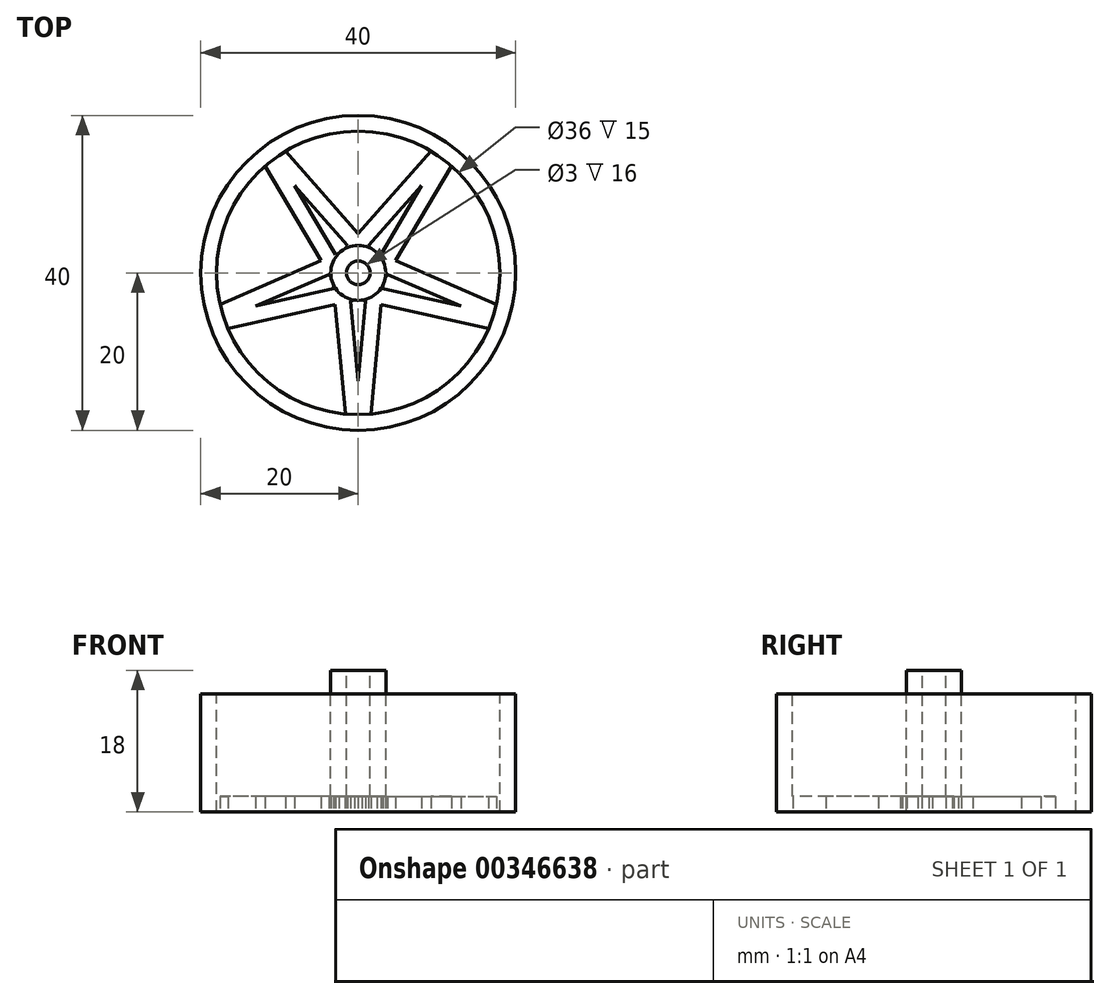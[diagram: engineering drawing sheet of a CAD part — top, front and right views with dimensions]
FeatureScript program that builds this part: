
annotation { "Feature Type Name" : "Feature", "Feature Type Description" : "" }
export const myFeature = defineFeature(function(context is Context, id is Id, definition is map)
    precondition{}
    {
        {
            var Q0;
            Q0=qCreatedBy(makeId("Top.planeOp"),FACE);
            var sketch = newSketch(context, id + "F0", { "sketchPlane" : qUnion([Q0])});
            skCircle(sketch, "E0", {"center": v(0, 0) * mm, "radius": 20 * mm});
            skSolve(sketch);
        }
        {
            var Q0;
            Q0=makeQuery(id+"F0.imprint","IMPRINT",FACE,{"disambiguationData":[TD([[makeQuery(id+"F0.imprint","IMPRINT",EDGE,{"derivedFrom":sQuery(id+"F0.wireOp",EDGE,"E0")}),1.0]])]});
            extrude(context, id + "F1", {"entities" : qUnion([Q0]), "depth" : 15 * mm});
        }
        {
            var Q0;
            Q0=makeQuery(id+"F1.opExtrude","CAP_FACE",FACE,{"disambiguationData":[OSD([sQuery(id+"F0.wireOp",EDGE,"E0")])],"isStart":false});
            var sketch = newSketch(context, id + "F2", { "sketchPlane" : qUnion([Q0])});
            skCircle(sketch, "E1", {"center": v(0, 0) * mm, "radius": 18 * mm});
            skSolve(sketch);
        }
        {
            var Q0;
            Q0=makeQuery(id+"F2.imprint","IMPRINT",FACE,{"disambiguationData":[TD([[makeQuery(id+"F2.imprint","IMPRINT",EDGE,{"derivedFrom":sQuery(id+"F2.wireOp",EDGE,"E1")}),1.0]])]});
            extrude(context, id + "F3", {"entities" : qUnion([Q0]), "operationType" : NewBodyOperationType.REMOVE, "oppositeDirection" : true, "depth" : 13 * mm});
        }
        {
            var Q0;
            Q0=makeQuery(id+"F2.imprint","IMPRINT",FACE,{"disambiguationData":[TD([[makeQuery(id+"F2.imprint","IMPRINT",EDGE,{"derivedFrom":sQuery(id+"F2.wireOp",EDGE,"E1")}),1.0]])]});
            var sketch = newSketch(context, id + "F4", { "sketchPlane" : qUnion([Q0])});
            skCircle(sketch, "E2", {"center": v(0, 0) * mm, "radius": 3.5 * mm});
            skCircle(sketch, "E3", {"center": v(0, 0) * mm, "radius": 1.5 * mm});
            skSolve(sketch);
        }
        {
            var Q0;
            Q0=makeQuery(id+"F4.imprint","IMPRINT",FACE,{"disambiguationData":[TD([[makeQuery(id+"F4.imprint","IMPRINT",EDGE,{"derivedFrom":sQuery(id+"F4.wireOp",EDGE,"E2")}),1.0]])]});
            extrude(context, id + "F5", {"entities" : qUnion([Q0]), "operationType" : NewBodyOperationType.ADD, "oppositeDirection" : true, "depth" : 13 * mm});
        }
        {
            var Q0;
            Q0=makeQuery(id+"F2.imprint","IMPRINT",FACE,{"disambiguationData":[TD([[makeQuery(id+"F2.imprint","IMPRINT",EDGE,{"derivedFrom":sQuery(id+"F2.wireOp",EDGE,"E1")}),1.0]])]});
            var sketch = newSketch(context, id + "F6", { "sketchPlane" : qUnion([Q0])});
            skCircle(sketch, "E4", {"center": v(0, 0) * mm, "radius": 1.5 * mm});
            skCircle(sketch, "E5", {"center": v(0, 0) * mm, "radius": 3.5 * mm});
            skSolve(sketch);
        }
        {
            var Q0;
            Q0=makeQuery(id+"F6.imprint","IMPRINT",FACE,{"disambiguationData":[TD([[makeQuery(id+"F6.imprint","IMPRINT",EDGE,{"derivedFrom":sQuery(id+"F6.wireOp",EDGE,"E4")}),-1.0]])]});
            extrude(context, id + "F7", {"entities" : qUnion([Q0]), "operationType" : NewBodyOperationType.ADD, "depth" : 3 * mm});
        }
        {
            var Q0;
            Q0=makeQuery(id+"F1.opExtrude","CAP_FACE",FACE,{"disambiguationData":[OSD([sQuery(id+"F0.wireOp",EDGE,"E0")])],"isStart":true});
            var sketch = newSketch(context, id + "F8", { "sketchPlane" : qUnion([Q0])});
            skSolve(sketch);
        }
        {
            var Q0;
            Q0=makeQuery(id+"F8.imprint","IMPRINT",FACE,{"disambiguationData":[TD([[makeQuery(id+"F8.imprint","IMPRINT",EDGE,{"derivedFrom":makeQuery(id+"F1.opExtrude","CAP_EDGE",EDGE,{"disambiguationData":[OSD([sQuery(id+"F0.wireOp",EDGE,"E0")])],"isStart":true})}),-1.0]])]});
            var sketch = newSketch(context, id + "F9", { "sketchPlane" : qUnion([Q0])});
            skCircle(sketch, "E6", {"center": v(0, 0) * mm, "radius": 3.5 * mm});
            skCircle(sketch, "E7", {"center": v(0, 0) * mm, "radius": 18 * mm});
            skLineSegment(sketch, "E8", {"start": v(-3.15, 1.52) * mm, "end": v(-3.1, 2.01) * mm});
            skLineSegment(sketch, "E9.MirrorCS", {"start": v(3.15, 1.52) * mm, "end": v(3.1, 2.01) * mm});
            skLineSegment(sketch, "E10.0", {"start": v(-0.97, 3.36) * mm, "end": v(0, 13.72) * mm});
            skLineSegment(sketch, "E11.0", {"start": v(0.97, 3.36) * mm, "end": v(0, 13.72) * mm});
            skLineSegment(sketch, "E12.1.0", {"start": v(-0.47, 3.47) * mm, "end": v(-0.95, 3.58) * mm});
            skLineSegment(sketch, "E12.1.1", {"start": v(-2.9, 1.96) * mm, "end": v(-13.05, 4.24) * mm});
            skLineSegment(sketch, "E12.1.2", {"start": v(-3.5, 0.11) * mm, "end": v(-13.05, 4.24) * mm});
            skLineSegment(sketch, "E12.1.3", {"start": v(-2.42, -2.53) * mm, "end": v(-2.87, -2.33) * mm});
            skLineSegment(sketch, "E12.2.0", {"start": v(-3.44, 0.63) * mm, "end": v(-3.7, 0.2) * mm});
            skLineSegment(sketch, "E12.2.1", {"start": v(-2.76, -2.15) * mm, "end": v(-8.07, -11.1) * mm});
            skLineSegment(sketch, "E12.2.2", {"start": v(-1.2, -3.3) * mm, "end": v(-8.07, -11.1) * mm});
            skLineSegment(sketch, "E12.2.3", {"start": v(1.66, -3.08) * mm, "end": v(1.33, -3.45) * mm});
            skLineSegment(sketch, "E12.3.0", {"start": v(-1.66, -3.08) * mm, "end": v(-1.33, -3.45) * mm});
            skLineSegment(sketch, "E12.3.1", {"start": v(1.2, -3.3) * mm, "end": v(8.07, -11.1) * mm});
            skLineSegment(sketch, "E12.3.2", {"start": v(2.76, -2.15) * mm, "end": v(8.07, -11.1) * mm});
            skLineSegment(sketch, "E12.3.3", {"start": v(3.44, 0.63) * mm, "end": v(3.7, 0.2) * mm});
            skLineSegment(sketch, "E12.4.0", {"start": v(2.42, -2.53) * mm, "end": v(2.87, -2.33) * mm});
            skLineSegment(sketch, "E12.4.1", {"start": v(3.5, 0.11) * mm, "end": v(13.05, 4.24) * mm});
            skLineSegment(sketch, "E12.4.2", {"start": v(2.9, 1.96) * mm, "end": v(13.05, 4.24) * mm});
            skLineSegment(sketch, "E12.4.3", {"start": v(0.47, 3.47) * mm, "end": v(0.95, 3.58) * mm});
            skLineSegment(sketch, "E13.trimOffspring", {"start": v(-2.92, 4.02) * mm, "end": v(-1.61, 17.93) * mm});
            skLineSegment(sketch, "E14.trimOffspring", {"start": v(-2.92, 4.02) * mm, "end": v(-16.55, 7.08) * mm});
            skLineSegment(sketch, "E15.trimOffspring", {"start": v(2.92, 4.02) * mm, "end": v(16.55, 7.08) * mm});
            skLineSegment(sketch, "E16.trimOffspring", {"start": v(2.92, 4.02) * mm, "end": v(1.61, 17.93) * mm});
            skLineSegment(sketch, "E17.trimOffspring", {"start": v(4.72, -1.53) * mm, "end": v(11.84, -13.55) * mm});
            skLineSegment(sketch, "E18.trimOffspring", {"start": v(4.72, -1.53) * mm, "end": v(17.55, 4) * mm});
            skLineSegment(sketch, "E19.trimOffspring", {"start": v(0, -4.97) * mm, "end": v(-9.23, -15.45) * mm});
            skLineSegment(sketch, "E20.trimOffspring", {"start": v(0, -4.97) * mm, "end": v(9.23, -15.45) * mm});
            skLineSegment(sketch, "E21.trimOffspring", {"start": v(-4.72, -1.53) * mm, "end": v(-17.55, 4) * mm});
            skLineSegment(sketch, "E22.trimOffspring", {"start": v(-4.72, -1.53) * mm, "end": v(-11.84, -13.55) * mm});
            skSolve(sketch);
        }
        {
            var Q0;
            {var subQ0=sQuery(id+"F9.wireOp",EDGE,"E13.trimOffspring");Q0=makeQuery(id+"F9.imprint","IMPRINT",FACE,{"disambiguationData":[TD([[makeQuery(id+"F9.imprint","IMPRINT",EDGE,{"derivedFrom":subQ0}),1.0]])]});}
            var Q1;
            {var subQ0=sQuery(id+"F9.wireOp",EDGE,"E21.trimOffspring");Q1=makeQuery(id+"F9.imprint","IMPRINT",FACE,{"disambiguationData":[TD([[makeQuery(id+"F9.imprint","IMPRINT",EDGE,{"derivedFrom":subQ0}),1.0]])]});}
            var Q2;
            {var subQ0=sQuery(id+"F9.wireOp",EDGE,"E19.trimOffspring");Q2=makeQuery(id+"F9.imprint","IMPRINT",FACE,{"disambiguationData":[TD([[makeQuery(id+"F9.imprint","IMPRINT",EDGE,{"derivedFrom":subQ0}),1.0]])]});}
            var Q3;
            {var subQ0=sQuery(id+"F9.wireOp",EDGE,"E17.trimOffspring");Q3=makeQuery(id+"F9.imprint","IMPRINT",FACE,{"disambiguationData":[TD([[makeQuery(id+"F9.imprint","IMPRINT",EDGE,{"derivedFrom":subQ0}),1.0]])]});}
            var Q4;
            {var subQ0=sQuery(id+"F9.wireOp",EDGE,"E15.trimOffspring");Q4=makeQuery(id+"F9.imprint","IMPRINT",FACE,{"disambiguationData":[TD([[makeQuery(id+"F9.imprint","IMPRINT",EDGE,{"derivedFrom":subQ0}),1.0]])]});}
            var Q5;
            {var subQ1=sQuery(id+"F9.wireOp",EDGE,"E12.1.3");Q5=makeQuery(id+"F9.imprint","IMPRINT",FACE,{"disambiguationData":[TD([[makeQuery(id+"F9.imprint","IMPRINT",EDGE,{"derivedFrom":subQ1}),1.0]])]});}
            var Q6;
            {var subQ1=sQuery(id+"F9.wireOp",EDGE,"E12.2.3");Q6=makeQuery(id+"F9.imprint","IMPRINT",FACE,{"disambiguationData":[TD([[makeQuery(id+"F9.imprint","IMPRINT",EDGE,{"derivedFrom":subQ1}),1.0]])]});}
            var Q7;
            {var subQ1=sQuery(id+"F9.wireOp",EDGE,"E9.MirrorCS");Q7=makeQuery(id+"F9.imprint","IMPRINT",FACE,{"disambiguationData":[TD([[makeQuery(id+"F9.imprint","IMPRINT",EDGE,{"derivedFrom":subQ1}),-1.0]])]});}
            var Q8;
            {var subQ0=sQuery(id+"F9.wireOp",EDGE,"E12.1.0");Q8=makeQuery(id+"F9.imprint","IMPRINT",FACE,{"disambiguationData":[TD([[makeQuery(id+"F9.imprint","IMPRINT",EDGE,{"derivedFrom":subQ0}),-1.0]])]});}
            var Q9;
            {var subQ1=sQuery(id+"F9.wireOp",EDGE,"E8");Q9=makeQuery(id+"F9.imprint","IMPRINT",FACE,{"disambiguationData":[TD([[makeQuery(id+"F9.imprint","IMPRINT",EDGE,{"derivedFrom":subQ1}),1.0]])]});}
            extrude(context, id + "F10", {"entities" : qUnion([Q0, Q1, Q2, Q3, Q4, Q5, Q6, Q7, Q8, Q9]), "operationType" : NewBodyOperationType.REMOVE, "oppositeDirection" : true, "depth" : 2 * mm});
        }
    });
